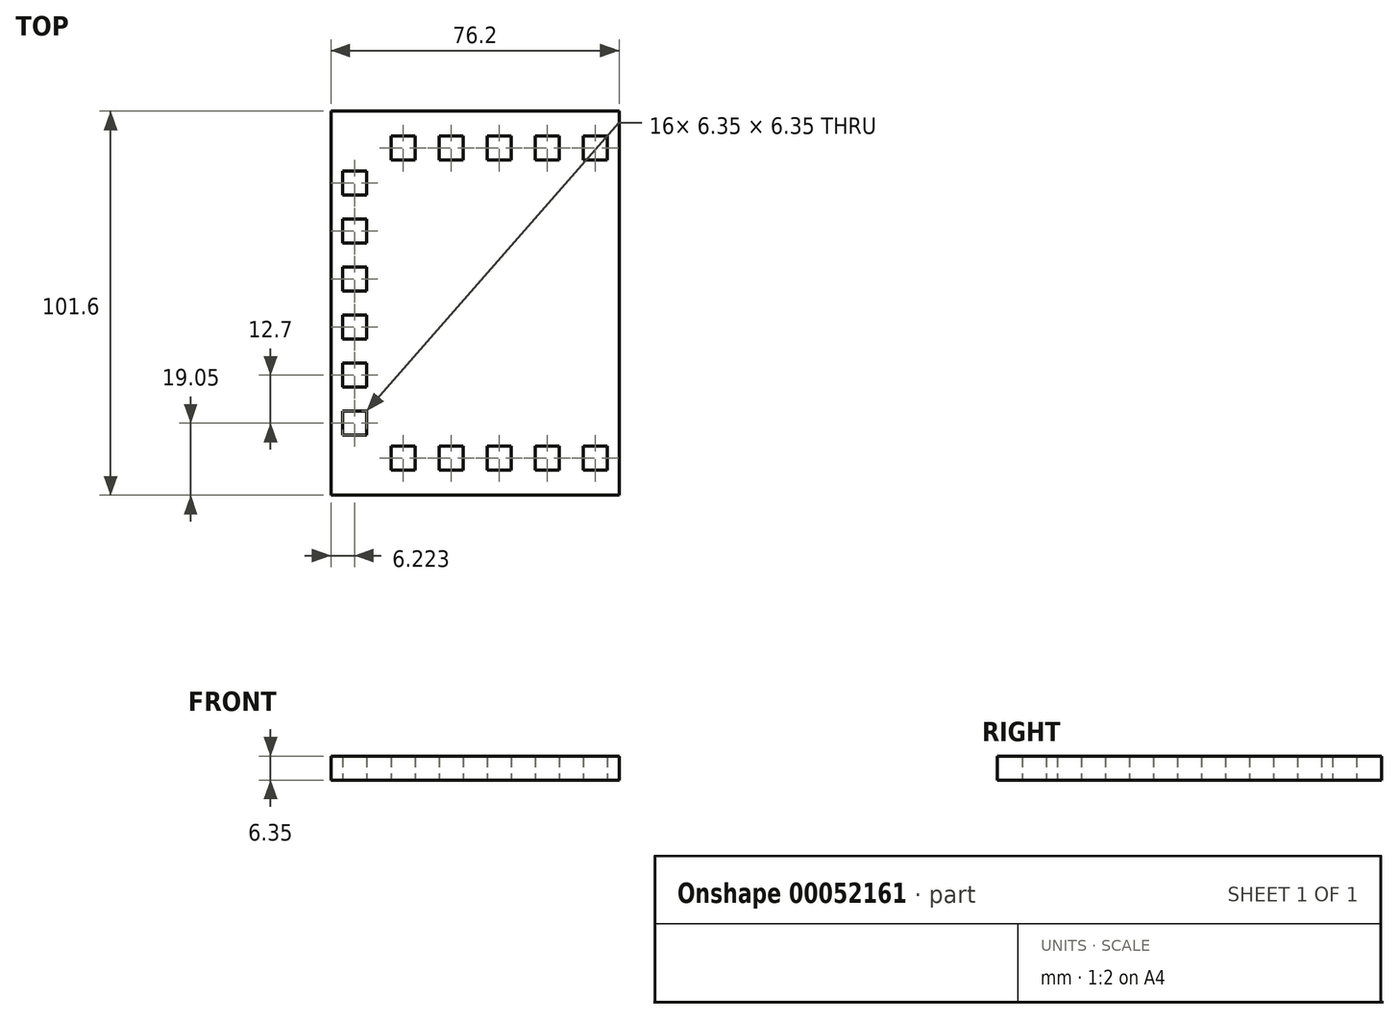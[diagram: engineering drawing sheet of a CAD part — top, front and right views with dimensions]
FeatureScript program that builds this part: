
annotation { "Feature Type Name" : "Feature", "Feature Type Description" : "" }
export const myFeature = defineFeature(function(context is Context, id is Id, definition is map)
    precondition{}
    {
        {
            var Q0;
            Q0=qCreatedBy(makeId("Top.planeOp"),FACE);
            var sketch = newSketch(context, id + "F0", { "sketchPlane" : qUnion([Q0])});
            skLineSegment(sketch, "E0.rect.bottom", {"start": v(38.1, 50.8) * mm, "end": v(-38.1, 50.8) * mm});
            skLineSegment(sketch, "E0.rect.top", {"start": v(38.1, -50.8) * mm, "end": v(-38.1, -50.8) * mm});
            skLineSegment(sketch, "E0.rect.left", {"start": v(38.1, 50.8) * mm, "end": v(38.1, -50.8) * mm});
            skLineSegment(sketch, "E0.rect.right", {"start": v(-38.1, 50.8) * mm, "end": v(-38.1, -50.8) * mm});
            skPoint(sketch, "E0.rect.middle", {"position": v(0, 0) * mm});
            skLineSegment(sketch, "E1.rect.bottom", {"start": v(28.57, 44.2) * mm, "end": v(34.93, 44.2) * mm});
            skLineSegment(sketch, "E1.rect.top", {"start": v(28.57, 37.85) * mm, "end": v(34.92, 37.85) * mm});
            skLineSegment(sketch, "E1.rect.left", {"start": v(28.57, 44.2) * mm, "end": v(28.57, 37.85) * mm});
            skLineSegment(sketch, "E1.rect.right", {"start": v(34.93, 44.2) * mm, "end": v(34.93, 37.85) * mm});
            skPoint(sketch, "E1.rect.middle", {"position": v(31.75, 41.02) * mm});
            skLineSegment(sketch, "E2.1.0.0", {"start": v(15.87, 37.85) * mm, "end": v(22.22, 37.85) * mm});
            skPoint(sketch, "E2.1.0.1", {"position": v(19.05, 41.02) * mm});
            skLineSegment(sketch, "E2.1.0.2", {"start": v(15.87, 44.2) * mm, "end": v(22.22, 44.2) * mm});
            skLineSegment(sketch, "E2.1.0.3", {"start": v(15.87, 44.2) * mm, "end": v(15.87, 37.85) * mm});
            skLineSegment(sketch, "E2.1.0.4", {"start": v(22.22, 44.2) * mm, "end": v(22.22, 37.85) * mm});
            skLineSegment(sketch, "E2.2.0.0", {"start": v(3.17, 37.85) * mm, "end": v(9.52, 37.85) * mm});
            skPoint(sketch, "E2.2.0.1", {"position": v(6.35, 41.02) * mm});
            skLineSegment(sketch, "E2.2.0.2", {"start": v(3.17, 44.2) * mm, "end": v(9.52, 44.2) * mm});
            skLineSegment(sketch, "E2.2.0.3", {"start": v(3.17, 44.2) * mm, "end": v(3.17, 37.85) * mm});
            skLineSegment(sketch, "E2.2.0.4", {"start": v(9.52, 44.2) * mm, "end": v(9.52, 37.85) * mm});
            skLineSegment(sketch, "E2.3.0.0", {"start": v(-9.53, 37.85) * mm, "end": v(-3.18, 37.85) * mm});
            skPoint(sketch, "E2.3.0.1", {"position": v(-6.35, 41.02) * mm});
            skLineSegment(sketch, "E2.3.0.2", {"start": v(-9.53, 44.2) * mm, "end": v(-3.18, 44.2) * mm});
            skLineSegment(sketch, "E2.3.0.3", {"start": v(-9.53, 44.2) * mm, "end": v(-9.53, 37.85) * mm});
            skLineSegment(sketch, "E2.3.0.4", {"start": v(-3.18, 44.2) * mm, "end": v(-3.18, 37.85) * mm});
            skLineSegment(sketch, "E2.4.0.0", {"start": v(-22.23, 37.85) * mm, "end": v(-15.88, 37.85) * mm});
            skPoint(sketch, "E2.4.0.1", {"position": v(-19.05, 41.02) * mm});
            skLineSegment(sketch, "E2.4.0.2", {"start": v(-22.23, 44.2) * mm, "end": v(-15.88, 44.2) * mm});
            skLineSegment(sketch, "E2.4.0.3", {"start": v(-22.23, 44.2) * mm, "end": v(-22.23, 37.85) * mm});
            skLineSegment(sketch, "E2.4.0.4", {"start": v(-15.88, 44.2) * mm, "end": v(-15.88, 37.85) * mm});
            skLineSegment(sketch, "E2.direction1", {"start": v(28.57, 37.85) * mm, "end": v(15.87, 37.85) * mm, "construction": true});
            skLineSegment(sketch, "E3.MirrorCS", {"start": v(-9.53, -44.2) * mm, "end": v(-3.18, -44.2) * mm});
            skLineSegment(sketch, "E4.MirrorCS", {"start": v(15.87, -37.85) * mm, "end": v(22.22, -37.85) * mm});
            skLineSegment(sketch, "E5.MirrorCS", {"start": v(-9.53, -37.85) * mm, "end": v(-3.18, -37.85) * mm});
            skLineSegment(sketch, "E6.MirrorCS", {"start": v(15.87, -44.2) * mm, "end": v(22.22, -44.2) * mm});
            skLineSegment(sketch, "E7.MirrorCS", {"start": v(28.57, -37.85) * mm, "end": v(15.87, -37.85) * mm, "construction": true});
            skLineSegment(sketch, "E8.MirrorCS", {"start": v(9.52, -44.2) * mm, "end": v(9.52, -37.85) * mm});
            skLineSegment(sketch, "E9.MirrorCS", {"start": v(-3.18, -44.2) * mm, "end": v(-3.18, -37.85) * mm});
            skLineSegment(sketch, "E10.MirrorCS", {"start": v(22.22, -44.2) * mm, "end": v(22.22, -37.85) * mm});
            skLineSegment(sketch, "E11.MirrorCS", {"start": v(15.87, -44.2) * mm, "end": v(15.87, -37.85) * mm});
            skLineSegment(sketch, "E12.MirrorCS", {"start": v(28.57, -44.2) * mm, "end": v(34.93, -44.2) * mm});
            skLineSegment(sketch, "E13.MirrorCS", {"start": v(-22.23, -44.2) * mm, "end": v(-22.23, -37.85) * mm});
            skLineSegment(sketch, "E14.MirrorCS", {"start": v(28.58, -44.2) * mm, "end": v(28.58, -37.85) * mm});
            skLineSegment(sketch, "E15.MirrorCS", {"start": v(28.57, -37.85) * mm, "end": v(34.92, -37.85) * mm});
            skLineSegment(sketch, "E16.MirrorCS", {"start": v(3.17, -44.2) * mm, "end": v(3.17, -37.85) * mm});
            skLineSegment(sketch, "E17.MirrorCS", {"start": v(-9.53, -44.2) * mm, "end": v(-9.53, -37.85) * mm});
            skLineSegment(sketch, "E18.MirrorCS", {"start": v(3.17, -37.85) * mm, "end": v(9.52, -37.85) * mm});
            skLineSegment(sketch, "E19.MirrorCS", {"start": v(3.17, -44.2) * mm, "end": v(9.52, -44.2) * mm});
            skLineSegment(sketch, "E20.MirrorCS", {"start": v(34.93, -44.2) * mm, "end": v(34.93, -37.85) * mm});
            skLineSegment(sketch, "E21.MirrorCS", {"start": v(-22.23, -37.85) * mm, "end": v(-15.88, -37.85) * mm});
            skLineSegment(sketch, "E22.MirrorCS", {"start": v(-22.23, -44.2) * mm, "end": v(-15.88, -44.2) * mm});
            skLineSegment(sketch, "E23.MirrorCS", {"start": v(-15.88, -44.2) * mm, "end": v(-15.88, -37.85) * mm});
            skPoint(sketch, "E24.MirrorP", {"position": v(-19.05, -41.02) * mm});
            skPoint(sketch, "E25.MirrorP", {"position": v(6.35, -41.02) * mm});
            skPoint(sketch, "E26.MirrorP", {"position": v(-6.35, -41.02) * mm});
            skPoint(sketch, "E27.MirrorP", {"position": v(31.75, -41.02) * mm});
            skPoint(sketch, "E28.MirrorP", {"position": v(19.05, -41.02) * mm});
            skLineSegment(sketch, "E29.bottom", {"start": v(-35.05, 3.17) * mm, "end": v(-28.7, 3.18) * mm});
            skLineSegment(sketch, "E29.top", {"start": v(-35.05, 9.53) * mm, "end": v(-28.7, 9.53) * mm});
            skLineSegment(sketch, "E29.left", {"start": v(-35.05, 3.18) * mm, "end": v(-35.05, 9.53) * mm});
            skLineSegment(sketch, "E29.right", {"start": v(-28.7, 3.18) * mm, "end": v(-28.7, 9.53) * mm});
            skLineSegment(sketch, "E30.0.1.0", {"start": v(-35.05, 22.23) * mm, "end": v(-28.7, 22.23) * mm});
            skLineSegment(sketch, "E30.0.1.1", {"start": v(-28.7, 15.88) * mm, "end": v(-28.7, 22.23) * mm});
            skLineSegment(sketch, "E30.0.1.2", {"start": v(-35.05, 15.88) * mm, "end": v(-28.7, 15.88) * mm});
            skLineSegment(sketch, "E30.0.1.3", {"start": v(-35.05, 15.88) * mm, "end": v(-35.05, 22.23) * mm});
            skLineSegment(sketch, "E30.0.2.0", {"start": v(-35.05, 34.93) * mm, "end": v(-28.7, 34.93) * mm});
            skLineSegment(sketch, "E30.0.2.1", {"start": v(-28.7, 28.57) * mm, "end": v(-28.7, 34.93) * mm});
            skLineSegment(sketch, "E30.0.2.2", {"start": v(-35.05, 28.57) * mm, "end": v(-28.7, 28.57) * mm});
            skLineSegment(sketch, "E30.0.2.3", {"start": v(-35.05, 28.57) * mm, "end": v(-35.05, 34.93) * mm});
            skLineSegment(sketch, "E30.direction1", {"start": v(-35.05, 9.53) * mm, "end": v(-9.65, 9.53) * mm, "construction": true});
            skLineSegment(sketch, "E30.direction2", {"start": v(-35.05, 9.53) * mm, "end": v(-35.05, 22.23) * mm, "construction": true});
            skLineSegment(sketch, "E31.MirrorCS", {"start": v(-35.05, -3.18) * mm, "end": v(-35.05, -9.53) * mm});
            skLineSegment(sketch, "E32.MirrorCS", {"start": v(-28.7, -28.57) * mm, "end": v(-28.7, -34.93) * mm});
            skLineSegment(sketch, "E33.MirrorCS", {"start": v(-35.05, -15.88) * mm, "end": v(-28.7, -15.88) * mm});
            skLineSegment(sketch, "E34.MirrorCS", {"start": v(-35.05, -28.57) * mm, "end": v(-28.7, -28.57) * mm});
            skLineSegment(sketch, "E35.MirrorCS", {"start": v(-35.05, -22.23) * mm, "end": v(-28.7, -22.23) * mm});
            skLineSegment(sketch, "E36.MirrorCS", {"start": v(-28.7, -15.88) * mm, "end": v(-28.7, -22.23) * mm});
            skLineSegment(sketch, "E37.MirrorCS", {"start": v(-35.05, -3.18) * mm, "end": v(-28.7, -3.17) * mm});
            skLineSegment(sketch, "E38.MirrorCS", {"start": v(-35.05, -15.88) * mm, "end": v(-35.05, -22.23) * mm});
            skLineSegment(sketch, "E39.MirrorCS", {"start": v(-35.05, -9.53) * mm, "end": v(-35.05, -22.23) * mm, "construction": true});
            skLineSegment(sketch, "E40.MirrorCS", {"start": v(-35.05, -9.53) * mm, "end": v(-9.65, -9.53) * mm, "construction": true});
            skLineSegment(sketch, "E41.MirrorCS", {"start": v(-28.7, -3.18) * mm, "end": v(-28.7, -9.53) * mm});
            skLineSegment(sketch, "E42.MirrorCS", {"start": v(-35.05, -34.93) * mm, "end": v(-28.7, -34.93) * mm});
            skLineSegment(sketch, "E43.MirrorCS", {"start": v(-35.05, -9.53) * mm, "end": v(-28.7, -9.53) * mm});
            skLineSegment(sketch, "E44.MirrorCS", {"start": v(-35.05, -28.57) * mm, "end": v(-35.05, -34.93) * mm});
            skSolve(sketch);
        }
        {
            var Q0;
            Q0=makeQuery(id+"F0.imprint","IMPRINT",FACE,{"disambiguationData":[TD([[makeQuery(id+"F0.imprint","IMPRINT",EDGE,{"derivedFrom":sQuery(id+"F0.wireOp",EDGE,"E0.rect.bottom")}),1.0]])]});
            extrude(context, id + "F1", {"entities" : qUnion([Q0]), "depth" : 6.35 * mm});
        }
    });
